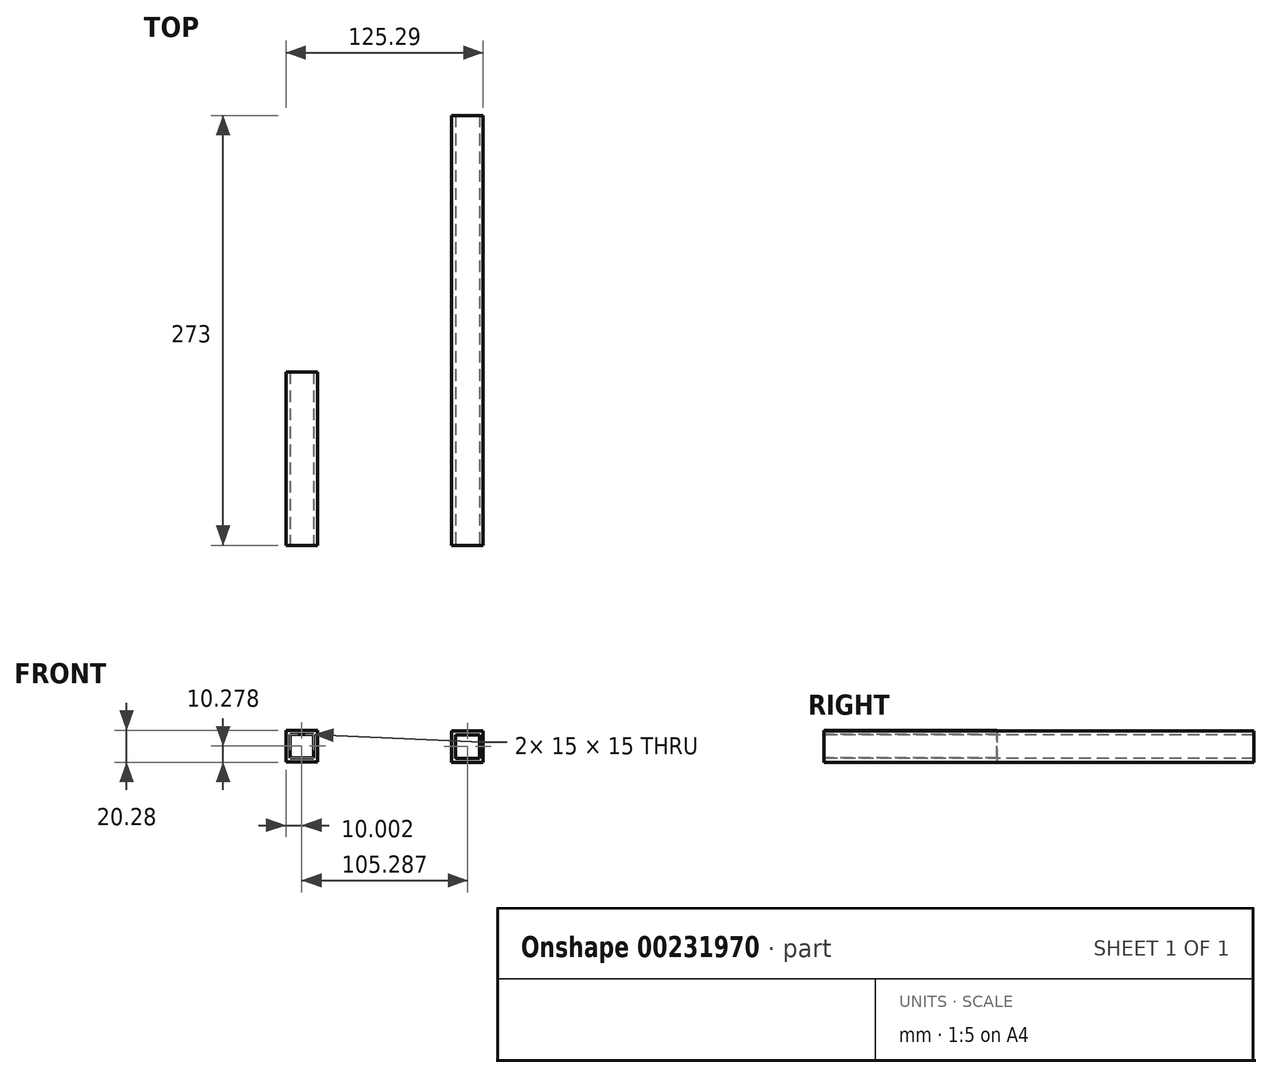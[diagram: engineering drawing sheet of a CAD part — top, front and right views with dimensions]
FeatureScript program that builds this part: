
annotation { "Feature Type Name" : "Feature", "Feature Type Description" : "" }
export const myFeature = defineFeature(function(context is Context, id is Id, definition is map)
    precondition{}
    {
        {
            var Q0;
            Q0=qCreatedBy(makeId("Front.planeOp"),FACE);
            var sketch = newSketch(context, id + "F0", { "sketchPlane" : qUnion([Q0])});
            skLineSegment(sketch, "E0.bottom", {"start": v(-66.3, 56.27) * mm, "end": v(-46.3, 56.27) * mm});
            skLineSegment(sketch, "E0.top", {"start": v(-66.3, 36.27) * mm, "end": v(-46.3, 36.27) * mm});
            skLineSegment(sketch, "E0.left", {"start": v(-66.3, 56.27) * mm, "end": v(-66.3, 36.27) * mm});
            skLineSegment(sketch, "E0.right", {"start": v(-46.3, 56.27) * mm, "end": v(-46.3, 36.27) * mm});
            skLineSegment(sketch, "E1.bottom", {"start": v(-48.8, 38.77) * mm, "end": v(-63.8, 38.77) * mm});
            skLineSegment(sketch, "E1.top", {"start": v(-48.8, 53.77) * mm, "end": v(-63.8, 53.77) * mm});
            skLineSegment(sketch, "E1.left", {"start": v(-48.8, 38.77) * mm, "end": v(-48.8, 53.77) * mm});
            skLineSegment(sketch, "E1.right", {"start": v(-63.8, 38.77) * mm, "end": v(-63.8, 53.77) * mm});
            skPoint(sketch, "E1.middle", {"position": v(-56.3, 46.27) * mm});
            skPoint(sketch, "E1.middle.positionSnap0", {"position": v(-66.3, 46.27) * mm});
            skPoint(sketch, "E1.middle.positionSnap1", {"position": v(-56.3, 56.27) * mm});
            skPoint(sketch, "E1.centerSnap0", {"position": v(-66.3, 46.27) * mm});
            skPoint(sketch, "E1.centerSnap1", {"position": v(-56.3, 56.27) * mm});
            skSolve(sketch);
        }
        {
            var Q0;
            Q0 = qSketchRegion(id + "F0", true);
            extrude(context, id + "F1", {"entities" : qUnion([Q0]), "oppositeDirection" : true, "depth" : 110 * mm});
        }
        {
            var Q0;
            Q0=qCreatedBy(makeId("Front.planeOp"),FACE);
            var sketch = newSketch(context, id + "F2", { "sketchPlane" : qUnion([Q0])});
            skLineSegment(sketch, "E2.bottom", {"start": v(38.98, 35.99) * mm, "end": v(58.98, 35.99) * mm});
            skLineSegment(sketch, "E2.top", {"start": v(38.98, 55.99) * mm, "end": v(58.98, 55.99) * mm});
            skLineSegment(sketch, "E2.left", {"start": v(38.98, 35.99) * mm, "end": v(38.98, 55.99) * mm});
            skLineSegment(sketch, "E2.right", {"start": v(58.98, 35.99) * mm, "end": v(58.98, 55.99) * mm});
            skPoint(sketch, "E2.middle", {"position": v(48.98, 45.99) * mm});
            skLineSegment(sketch, "E3.bottom", {"start": v(56.48, 38.49) * mm, "end": v(41.48, 38.49) * mm});
            skLineSegment(sketch, "E3.top", {"start": v(56.48, 53.49) * mm, "end": v(41.48, 53.49) * mm});
            skLineSegment(sketch, "E3.left", {"start": v(56.48, 38.49) * mm, "end": v(56.48, 53.49) * mm});
            skLineSegment(sketch, "E3.right", {"start": v(41.48, 38.49) * mm, "end": v(41.48, 53.49) * mm});
            skSolve(sketch);
        }
        {
            var Q0;
            Q0=makeQuery(id+"F2.imprint","IMPRINT",FACE,{"disambiguationData":[TD([[makeQuery(id+"F2.imprint","IMPRINT",EDGE,{"derivedFrom":sQuery(id+"F2.wireOp",EDGE,"E2.bottom")}),1.0]])]});
            extrude(context, id + "F3", {"entities" : qUnion([Q0]), "oppositeDirection" : true, "depth" : 273 * mm});
        }
    });
